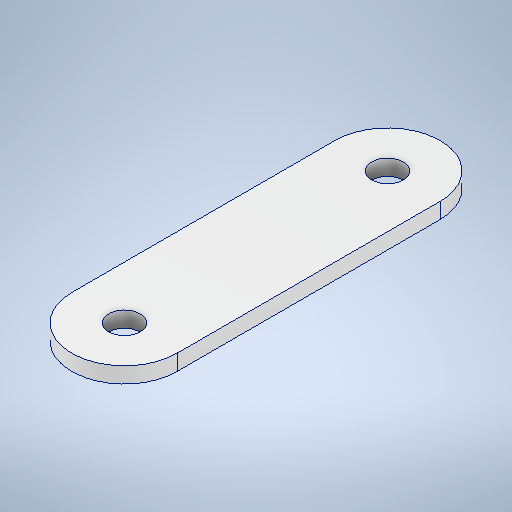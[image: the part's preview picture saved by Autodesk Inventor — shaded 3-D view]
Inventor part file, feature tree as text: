
AUTODESK INVENTOR PART (.ipt)
format: ipt  version: 2025 (Build 290162000, 162)  size: 249,856 bytes
history: native  units: mm
features: sketch x2, other x1, extrude x1, hole x1, projected_geometry x1
ambient origin geometry x8: Origin, YZ Plane, XZ Plane, XY Plane, X Axis, Y Axis, Z Axis, Center Point
bodies: Body1 (feature_tree)
feature tree (6):
  other  "Těleso1"
  extrude  "Vysunutí1"  Depth=10.0mm
  hole  "Díra1"  [1 undecoded]
  sketch  "Náčrt1"
  sketch  "Náčrt2"
  projected_geometry  "Promítnutá smyčka1"
note: 1 required parameter value undecoded (feature->parameter linkage not recoverable at this tier; creation-order binding heuristic only, values carry confidence <= 0.55)
